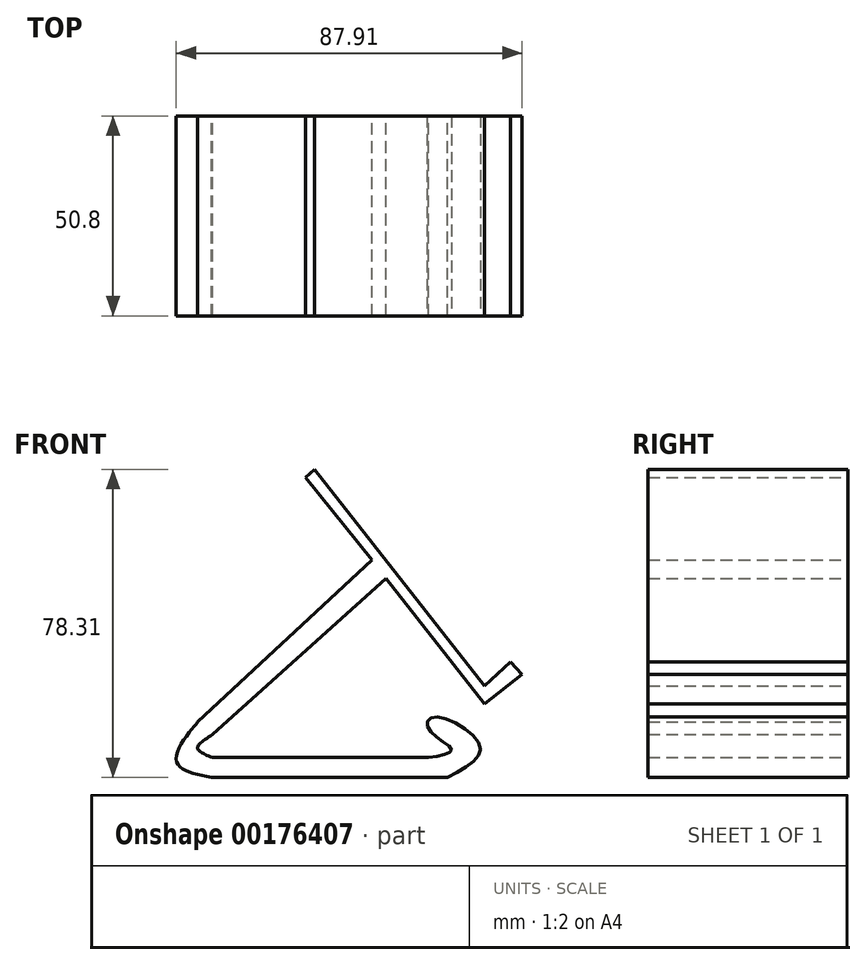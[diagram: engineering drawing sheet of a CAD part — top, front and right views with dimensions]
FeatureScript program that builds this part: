
annotation { "Feature Type Name" : "Feature", "Feature Type Description" : "" }
export const myFeature = defineFeature(function(context is Context, id is Id, definition is map)
    precondition{}
    {
        {
            var Q0;
            Q0=qCreatedBy(makeId("Front.planeOp"),FACE);
            var sketch = newSketch(context, id + "F0", { "sketchPlane" : qUnion([Q0])});
            skFitSpline(sketch, "E0", {"points": [v(-34.25, -30.03) * mm, v(-38, -27.63) * mm, v(-34.25, -24.18) * mm], "startDerivative": vector(-11.36, 4.56) * mm, "endDerivative": vector(11.11, 7.12) * mm});
            skFitSpline(sketch, "E1", {"points": [v(-34.54, -35.11) * mm, v(-43.46, -30.03) * mm, v(-38, -21) * mm, v(-38.28, -21.3) * mm], "startDerivative": vector(-30.29, 6.24) * mm, "endDerivative": vector(-5.32, -5.5) * mm});
            skLineSegment(sketch, "E2", {"start": v(-38, -21) * mm, "end": v(6.33, 20.15) * mm});
            skLineSegment(sketch, "E3", {"start": v(-34.25, -24.18) * mm, "end": v(9.79, 15.54) * mm});
            skLineSegment(sketch, "E4", {"start": v(9.79, 15.54) * mm, "end": v(34.82, -16.4) * mm});
            skLineSegment(sketch, "E5", {"start": v(34.82, -16.4) * mm, "end": v(44.44, -8.87) * mm});
            skLineSegment(sketch, "E6", {"start": v(44.44, -8.87) * mm, "end": v(41.48, -5.68) * mm});
            skLineSegment(sketch, "E7", {"start": v(41.48, -5.68) * mm, "end": v(34.82, -11.86) * mm});
            skLineSegment(sketch, "E8", {"start": v(34.82, -11.86) * mm, "end": v(-8.33, 43.2) * mm});
            skLineSegment(sketch, "E9", {"start": v(-8.33, 43.2) * mm, "end": v(-10.6, 41.1) * mm});
            skLineSegment(sketch, "E10", {"start": v(-10.6, 41.1) * mm, "end": v(6.33, 20.15) * mm});
            skLineSegment(sketch, "E11", {"start": v(-34.25, -30.03) * mm, "end": v(20.63, -30.03) * mm});
            skLineSegment(sketch, "E12", {"start": v(-34.54, -35.11) * mm, "end": v(25.47, -35.11) * mm});
            skFitSpline(sketch, "E13", {"points": [v(20.63, -30.03) * mm, v(26.44, -28) * mm, v(20.63, -22.67) * mm, v(21.92, -19.77) * mm, v(33.71, -27.04) * mm, v(25.47, -35.11) * mm], "startDerivative": vector(51.71, 8.07) * mm, "endDerivative": vector(-57.36, -30.8) * mm});
            skSolve(sketch);
        }
        {
            var Q0;
            Q0=makeQuery(id+"F0.imprint","IMPRINT",FACE,{"disambiguationData":[TD([[makeQuery(id+"F0.imprint","IMPRINT",EDGE,{"derivedFrom":sQuery(id+"F0.wireOp",EDGE,"E0")}),1.0]])]});
            extrude(context, id + "F1", {"entities" : qUnion([Q0]), "depth" : 50.8 * mm});
        }
    });
